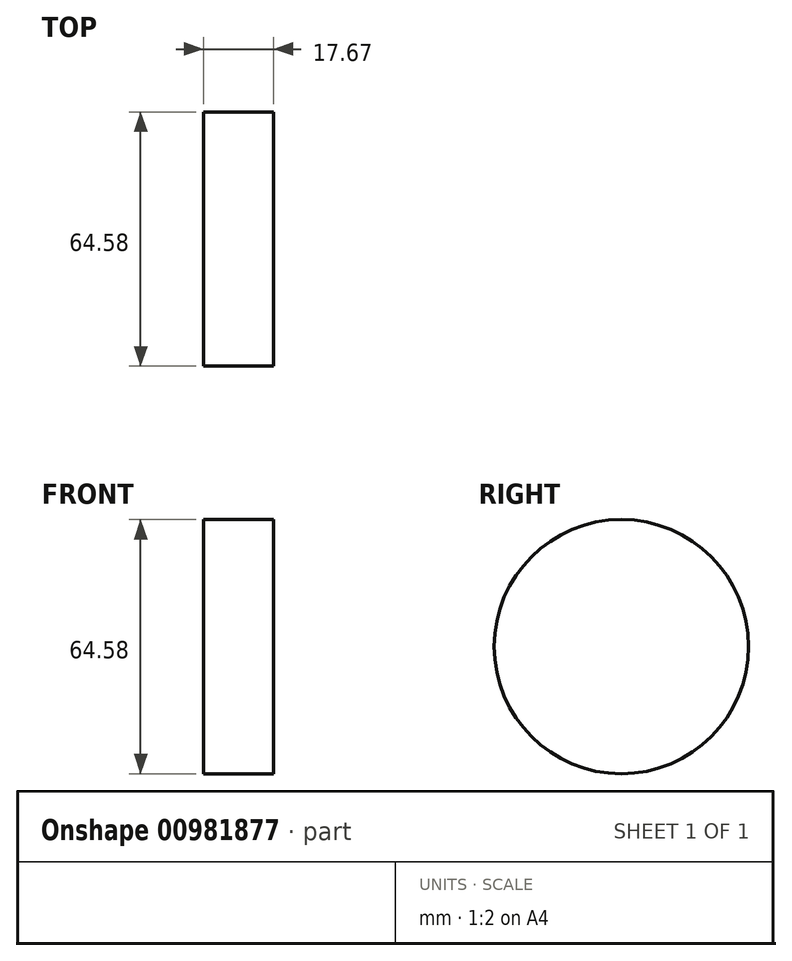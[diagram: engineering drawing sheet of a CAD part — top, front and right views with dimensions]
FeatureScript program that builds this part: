
annotation { "Feature Type Name" : "Feature", "Feature Type Description" : "" }
export const myFeature = defineFeature(function(context is Context, id is Id, definition is map)
    precondition{}
    {
        {
            var Q0;
            Q0=qCreatedBy(makeId("Right.planeOp"),FACE);
            var sketch = newSketch(context, id + "F0", { "sketchPlane" : qUnion([Q0])});
            skCircle(sketch, "E0", {"center": v(-57.9, 49.2) * mm, "radius": 32.3 * mm});
            skSolve(sketch);
        }
        {
            var Q0;
            Q0=makeQuery(id+"F0.imprint","IMPRINT",FACE,{"disambiguationData":[TD([[makeQuery(id+"F0.imprint","IMPRINT",EDGE,{"derivedFrom":sQuery(id+"F0.wireOp",EDGE,"E0")}),1.0]])]});
            extrude(context, id + "F1", {"entities" : qUnion([Q0]), "depth" : 17.67 * mm, "offsetDistance" : 25.4 * mm});
        }
    });
